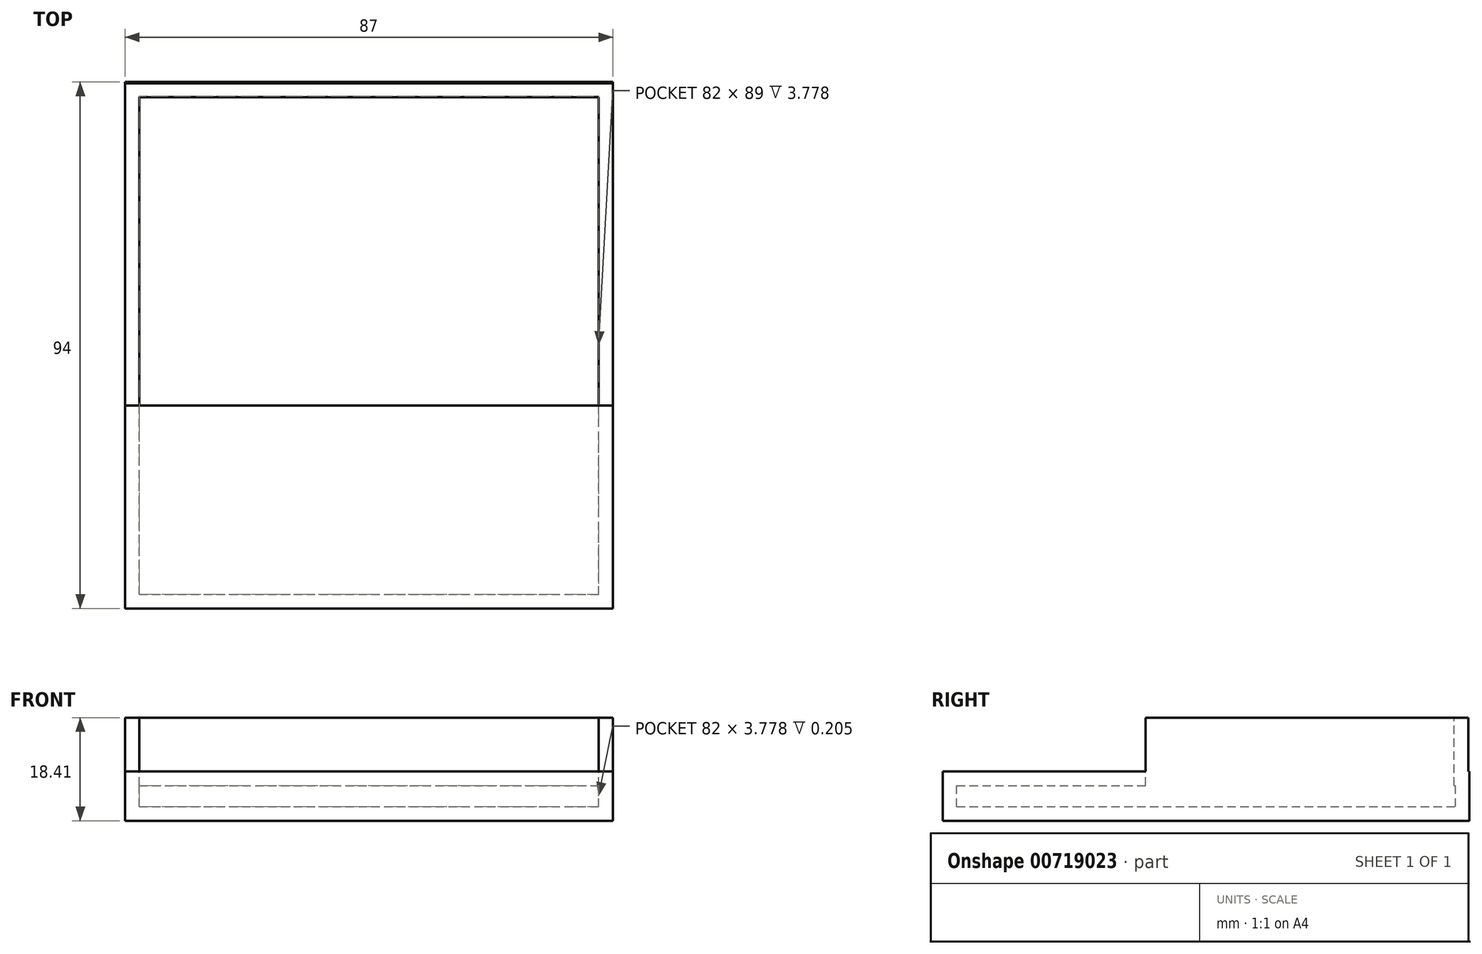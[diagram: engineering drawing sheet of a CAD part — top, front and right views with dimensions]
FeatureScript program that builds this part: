
annotation { "Feature Type Name" : "Feature", "Feature Type Description" : "" }
export const myFeature = defineFeature(function(context is Context, id is Id, definition is map)
    precondition{}
    {
        {
            var Q0;
            Q0=qCreatedBy(makeId("Front.planeOp"),FACE);
            var sketch = newSketch(context, id + "F0", { "sketchPlane" : qUnion([Q0])});
            skLineSegment(sketch, "E0.bottom", {"start": v(-43.5, -4.39) * mm, "end": v(43.5, -4.39) * mm});
            skLineSegment(sketch, "E0.top", {"start": v(-43.5, 4.39) * mm, "end": v(43.5, 4.39) * mm});
            skLineSegment(sketch, "E0.left", {"start": v(-43.5, -4.39) * mm, "end": v(-43.5, 4.39) * mm});
            skLineSegment(sketch, "E0.right", {"start": v(43.5, -4.39) * mm, "end": v(43.5, 4.39) * mm});
            skPoint(sketch, "E0.middle", {"position": v(0, 0) * mm});
            skSolve(sketch);
        }
        {
            var Q0;
            Q0=makeQuery(id+"F0.imprint","IMPRINT",FACE,{"disambiguationData":[TD([[makeQuery(id+"F0.imprint","IMPRINT",EDGE,{"derivedFrom":sQuery(id+"F0.wireOp",EDGE,"E0.bottom")}),1.0]])]});
            extrude(context, id + "F1", {"entities" : qUnion([Q0]), "depth" : 47 * mm, "offsetDistance" : 25 * mm, "hasSecondDirection" : true, "secondDirectionOppositeDirection" : true, "secondDirectionDepth" : 47 * mm});
        }
        {
            var Q0;
            Q0=qCreatedBy(makeId("Right.planeOp"),FACE);
            var sketch = newSketch(context, id + "F2", { "sketchPlane" : qUnion([Q0])});
            skLineSegment(sketch, "E1.bottom", {"start": v(46.8, 0) * mm, "end": v(-10.78, 0) * mm});
            skLineSegment(sketch, "E1.top", {"start": v(46.8, 14.02) * mm, "end": v(-10.78, 14.02) * mm});
            skLineSegment(sketch, "E1.left", {"start": v(46.8, 0) * mm, "end": v(46.8, 14.02) * mm});
            skLineSegment(sketch, "E1.right", {"start": v(-10.78, 0) * mm, "end": v(-10.78, 14.02) * mm});
            skSolve(sketch);
        }
        {
            var Q0;
            Q0=makeQuery(id+"F2.imprint","IMPRINT",FACE,{"disambiguationData":[TD([[makeQuery(id+"F2.imprint","IMPRINT",EDGE,{"derivedFrom":sQuery(id+"F2.wireOp",EDGE,"E1.bottom")}),-1.0]])]});
            extrude(context, id + "F3", {"entities" : qUnion([Q0]), "operationType" : NewBodyOperationType.ADD, "depth" : 43.5 * mm, "offsetDistance" : 25 * mm, "hasSecondDirection" : true, "secondDirectionOppositeDirection" : true, "secondDirectionDepth" : 43.5 * mm});
        }
        {
            var Q0;
            Q0=makeQuery(id+"F3.opExtrude","SWEPT_FACE",FACE,{"disambiguationData":[OSD([sQuery(id+"F2.wireOp",EDGE,"E1.top")])]});
            var Q1;
            Q1=makeQuery(id+"F3.opExtrude","SWEPT_FACE",FACE,{"disambiguationData":[OSD([sQuery(id+"F2.wireOp",EDGE,"E1.right")])]});
            shell(context, id + "F4", {"entities" : qUnion([Q0, Q1]), "thickness" : 2.5 * mm});
        }
        {
            var Q0;
            Q0=qCreatedBy(makeId("Top.planeOp"),FACE);
            var sketch = newSketch(context, id + "F5", { "sketchPlane" : qUnion([Q0])});
            skCircle(sketch, "E2", {"center": v(0, 0) * mm, "radius": 33.17 * mm});
            skSolve(sketch);
        }
        {
            var Q0;
            Q0=sQuery(id+"F5.wireOp",EDGE,"E2");
            extrude(context, id + "F6", {"bodyType" : ToolBodyType.SURFACE, "surfaceEntities" : qUnion([Q0]), "depth" : 15 * mm, "offsetDistance" : 25 * mm});
        }
    });
